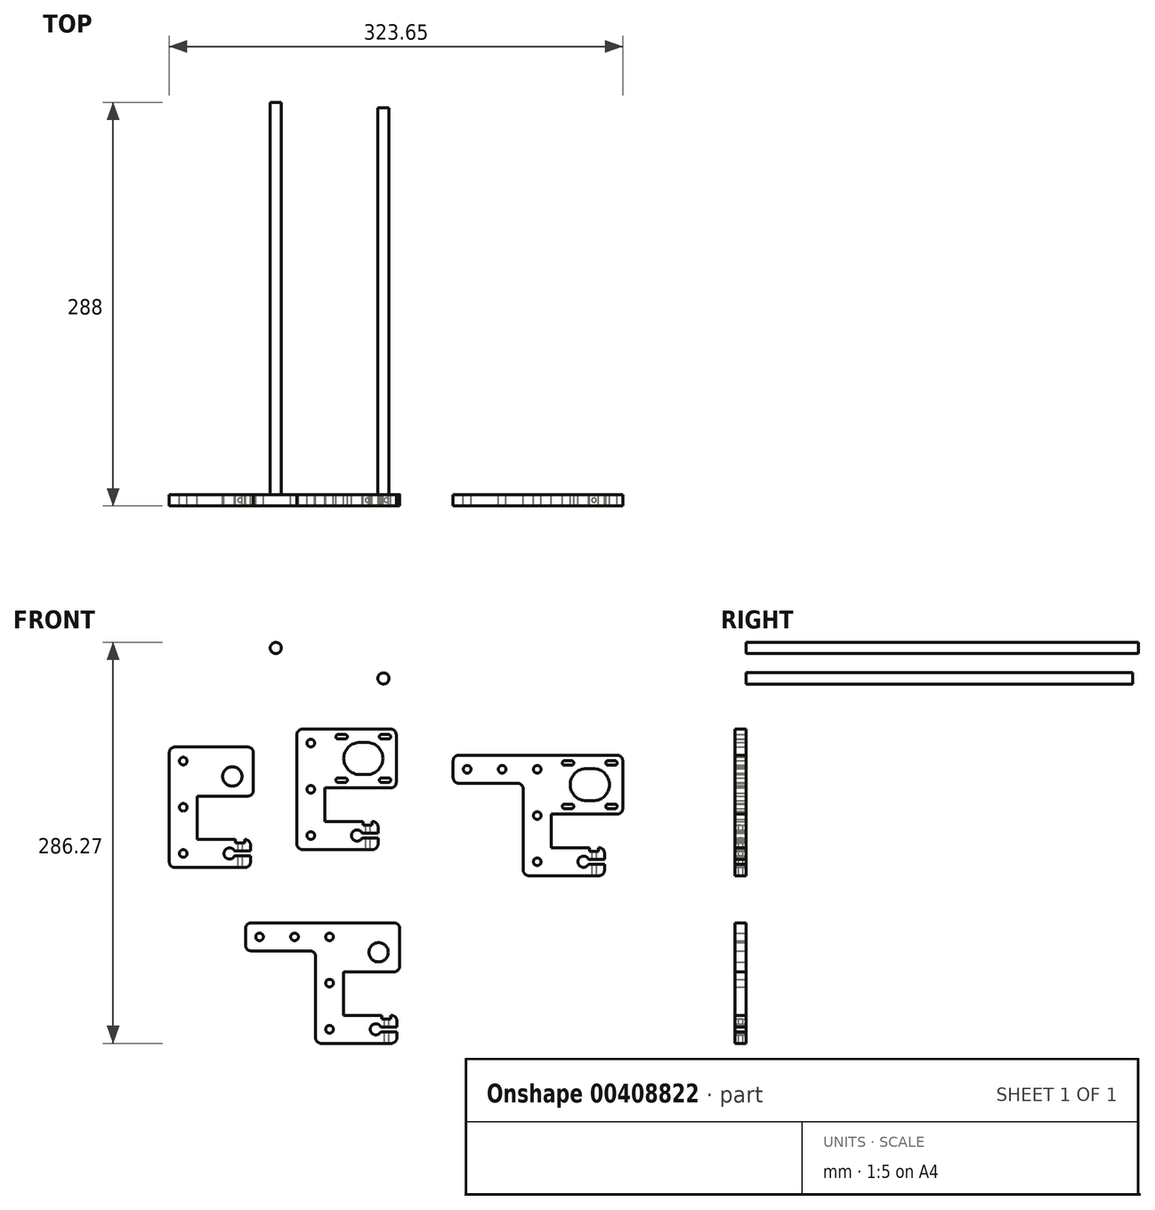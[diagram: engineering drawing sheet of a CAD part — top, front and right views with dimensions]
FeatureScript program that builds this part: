
annotation { "Feature Type Name" : "Feature", "Feature Type Description" : "" }
export const myFeature = defineFeature(function(context is Context, id is Id, definition is map)
    precondition{}
    {
        {
            var Q0;
            Q0=qCreatedBy(makeId("Front.planeOp"),FACE);
            var sketch = newSketch(context, id + "F0", { "sketchPlane" : qUnion([Q0])});
            skLineSegment(sketch, "E0", {"start": v(-154.16, 11) * mm, "end": v(-154.16, -55) * mm, "construction": true});
            skLineSegment(sketch, "E1", {"start": v(-179.8, 0) * mm, "end": v(-87.6, 0) * mm, "construction": true});
            skLineSegment(sketch, "E2", {"start": v(-97.16, 21) * mm, "end": v(-160.16, 21) * mm});
            skLineSegment(sketch, "E3", {"start": v(-164.16, 17) * mm, "end": v(-164.16, -61) * mm});
            skLineSegment(sketch, "E4", {"start": v(-160.16, -65) * mm, "end": v(-110.16, -65) * mm});
            skLineSegment(sketch, "E5", {"start": v(-106.16, -61) * mm, "end": v(-106.16, -56.75) * mm});
            skLineSegment(sketch, "E6", {"start": v(-93.16, 17) * mm, "end": v(-93.16, -17) * mm});
            skLineSegment(sketch, "E7", {"start": v(-97.16, -21) * mm, "end": v(-144.16, -21) * mm});
            skLineSegment(sketch, "E8", {"start": v(-144.16, -21) * mm, "end": v(-144.16, -45) * mm});
            skLineSegment(sketch, "E9", {"start": v(-144.16, -45) * mm, "end": v(-110.16, -45) * mm});
            skLineSegment(sketch, "E10", {"start": v(-106.16, -49) * mm, "end": v(-106.16, -53.25) * mm});
            skLineSegment(sketch, "E11", {"start": v(-142.74, -55) * mm, "end": v(-86.15, -55) * mm, "construction": true});
            skLineSegment(sketch, "E12", {"start": v(-106.16, -53.25) * mm, "end": v(-117.56, -53.25) * mm});
            skLineSegment(sketch, "E13", {"start": v(-106.16, -56.75) * mm, "end": v(-117.56, -56.75) * mm});
            skArc(sketch, "E14", {"start": v(-117.56, -53.25) * mm, "mid": v(-125.16, -55) * mm, "end": v(-117.56, -56.75) * mm});
            skCircle(sketch, "E15", {"center": v(-154.16, 11) * mm, "radius": 2.75 * mm});
            skCircle(sketch, "E16", {"center": v(-154.16, -22) * mm, "radius": 2.75 * mm});
            skCircle(sketch, "E17", {"center": v(-154.16, -55) * mm, "radius": 2.75 * mm});
            skLineSegment(sketch, "E18", {"start": v(-119.16, 0) * mm, "end": v(-114.16, 0) * mm, "construction": true});
            skArc(sketch, "E19.0.startCap", {"start": v(-119.16, -11.5) * mm, "mid": v(-130.66, 0) * mm, "end": v(-119.16, 11.5) * mm});
            skArc(sketch, "E19.0.endCap", {"start": v(-114.16, 11.5) * mm, "mid": v(-102.66, 0) * mm, "end": v(-114.16, -11.5) * mm});
            skLineSegment(sketch, "E19.0.left", {"start": v(-119.16, 11.5) * mm, "end": v(-114.16, 11.5) * mm});
            skLineSegment(sketch, "E19.0.right", {"start": v(-119.16, -11.5) * mm, "end": v(-114.16, -11.5) * mm});
            skPoint(sketch, "E20.visualSharp", {"position": v(-164.16, 21) * mm});
            skArc(sketch, "E20.filletArc", {"start": v(-160.16, 21) * mm, "mid": v(-162.99, 19.83) * mm, "end": v(-164.16, 17) * mm});
            skPoint(sketch, "E21.visualSharp", {"position": v(-93.16, 21) * mm});
            skArc(sketch, "E21.filletArc", {"start": v(-93.16, 17) * mm, "mid": v(-94.33, 19.83) * mm, "end": v(-97.16, 21) * mm});
            skPoint(sketch, "E22.visualSharp", {"position": v(-93.16, -21) * mm});
            skArc(sketch, "E22.filletArc", {"start": v(-97.16, -21) * mm, "mid": v(-94.33, -19.83) * mm, "end": v(-93.16, -17) * mm});
            skPoint(sketch, "E23.visualSharp", {"position": v(-106.16, -45) * mm});
            skArc(sketch, "E23.filletArc", {"start": v(-106.16, -49) * mm, "mid": v(-107.33, -46.17) * mm, "end": v(-110.16, -45) * mm});
            skPoint(sketch, "E24.visualSharp", {"position": v(-106.16, -65) * mm});
            skArc(sketch, "E24.filletArc", {"start": v(-110.16, -65) * mm, "mid": v(-107.33, -63.83) * mm, "end": v(-106.16, -61) * mm});
            skPoint(sketch, "E25.visualSharp", {"position": v(-164.16, -65) * mm});
            skArc(sketch, "E25.filletArc", {"start": v(-164.16, -61) * mm, "mid": v(-162.99, -63.83) * mm, "end": v(-160.16, -65) * mm});
            skLineSegment(sketch, "E26", {"start": v(-103.66, 15.5) * mm, "end": v(-98.66, 15.5) * mm, "construction": true});
            skArc(sketch, "E27.0.startCap", {"start": v(-103.66, 13.9) * mm, "mid": v(-105.26, 15.5) * mm, "end": v(-103.66, 17.1) * mm});
            skArc(sketch, "E27.0.endCap", {"start": v(-98.66, 17.1) * mm, "mid": v(-97.06, 15.5) * mm, "end": v(-98.66, 13.9) * mm});
            skLineSegment(sketch, "E27.0.left", {"start": v(-103.66, 17.1) * mm, "end": v(-98.66, 17.1) * mm});
            skLineSegment(sketch, "E27.0.right", {"start": v(-103.66, 13.9) * mm, "end": v(-98.66, 13.9) * mm});
            skLineSegment(sketch, "E28", {"start": v(-114.16, 23) * mm, "end": v(-114.16, -15.65) * mm, "construction": true});
            skLineSegment(sketch, "E29", {"start": v(-116.66, -11.5) * mm, "end": v(-116.66, 11.5) * mm, "construction": true});
            skArc(sketch, "E30.MirrorCS", {"start": v(-129.66, 13.9) * mm, "mid": v(-128.06, 15.5) * mm, "end": v(-129.66, 17.1) * mm});
            skArc(sketch, "E31.MirrorCS", {"start": v(-134.66, 17.1) * mm, "mid": v(-136.26, 15.5) * mm, "end": v(-134.66, 13.9) * mm});
            skLineSegment(sketch, "E32.MirrorCS", {"start": v(-129.66, 13.9) * mm, "end": v(-134.66, 13.9) * mm});
            skLineSegment(sketch, "E33.MirrorCS", {"start": v(-129.66, 15.5) * mm, "end": v(-134.66, 15.5) * mm, "construction": true});
            skLineSegment(sketch, "E34.MirrorCS", {"start": v(-129.66, 17.1) * mm, "end": v(-134.66, 17.1) * mm});
            skLineSegment(sketch, "E35.MirrorCS", {"start": v(-103.66, -13.9) * mm, "end": v(-98.66, -13.9) * mm});
            skArc(sketch, "E36.MirrorCS", {"start": v(-98.66, -17.1) * mm, "mid": v(-97.06, -15.5) * mm, "end": v(-98.66, -13.9) * mm});
            skArc(sketch, "E37.MirrorCS", {"start": v(-129.66, -13.9) * mm, "mid": v(-128.06, -15.5) * mm, "end": v(-129.66, -17.1) * mm});
            skLineSegment(sketch, "E38.MirrorCS", {"start": v(-103.66, -17.1) * mm, "end": v(-98.66, -17.1) * mm});
            skArc(sketch, "E39.MirrorCS", {"start": v(-134.66, -17.1) * mm, "mid": v(-136.26, -15.5) * mm, "end": v(-134.66, -13.9) * mm});
            skArc(sketch, "E40.MirrorCS", {"start": v(-103.66, -13.9) * mm, "mid": v(-105.26, -15.5) * mm, "end": v(-103.66, -17.1) * mm});
            skLineSegment(sketch, "E41.MirrorCS", {"start": v(-103.66, -15.5) * mm, "end": v(-98.66, -15.5) * mm, "construction": true});
            skLineSegment(sketch, "E42.MirrorCS", {"start": v(-129.66, -13.9) * mm, "end": v(-134.66, -13.9) * mm});
            skLineSegment(sketch, "E43.MirrorCS", {"start": v(-129.66, -15.5) * mm, "end": v(-134.66, -15.5) * mm, "construction": true});
            skLineSegment(sketch, "E44.MirrorCS", {"start": v(-129.66, -17.1) * mm, "end": v(-134.66, -17.1) * mm});
            skSolve(sketch);
        }
        {
            var Q0;
            Q0 = qSketchRegion(id + "F0", true);
            var Q1;
            Q1=makeQuery(id+"F0.imprint","IMPRINT",FACE,{"disambiguationData":[TD([[makeQuery(id+"F0.imprint","IMPRINT",EDGE,{"derivedFrom":sQuery(id+"F0.wireOp",EDGE,"E2")}),1.0]])]});
            extrude(context, id + "F1", {"entities" : qUnion([Q0, Q1]), "depth" : 8 * mm});
        }
        {
            var Q0;
            Q0=makeQuery(id+"F1.opExtrude","SWEPT_FACE",FACE,{"disambiguationData":[OSD([sQuery(id+"F0.wireOp",EDGE,"E4")])]});
            var sketch = newSketch(context, id + "F2", { "sketchPlane" : qUnion([Q0])});
            skLineSegment(sketch, "E45", {"start": v(-160.16, 4) * mm, "end": v(-110.16, 4) * mm, "construction": true});
            skCircle(sketch, "E46", {"center": v(-113.66, 4) * mm, "radius": 1.6 * mm});
            skSolve(sketch);
        }
        {
            var Q0;
            Q0 = qSketchRegion(id + "F2", true);
            var Q1;
            Q1=makeQuery(id+"F1.opExtrude","SWEPT_FACE",FACE,{"disambiguationData":[OSD([sQuery(id+"F0.wireOp",EDGE,"E9")])]});
            extrude(context, id + "F3", {"entities" : qUnion([Q0]), "operationType" : NewBodyOperationType.REMOVE, "endBound" : BoundingType.UP_TO_SURFACE, "oppositeDirection" : true, "endBoundEntityFace" : qUnion([Q1]), "depth" : 25 * mm});
        }
        {
            var Q0;
            Q0=makeQuery(id+"F1.opExtrude","SWEPT_FACE",FACE,{"disambiguationData":[OSD([sQuery(id+"F0.wireOp",EDGE,"E9")])]});
            var sketch = newSketch(context, id + "F4", { "sketchPlane" : qUnion([Q0])});
            skCircle(sketch, "E47.0", {"center": v(-113.66, -4) * mm, "radius": 1.6 * mm, "construction": true});
            skLineSegment(sketch, "E48.bottom", {"start": v(-110.4, -8) * mm, "end": v(-116.9, -8) * mm});
            skLineSegment(sketch, "E48.top", {"start": v(-110.4, 0) * mm, "end": v(-116.9, 0) * mm});
            skLineSegment(sketch, "E48.left", {"start": v(-110.4, -8) * mm, "end": v(-110.4, 0) * mm});
            skLineSegment(sketch, "E48.right", {"start": v(-116.9, -8) * mm, "end": v(-116.9, 0) * mm});
            skSolve(sketch);
        }
        {
            var Q0;
            Q0 = qSketchRegion(id + "F4", true);
            extrude(context, id + "F5", {"entities" : qUnion([Q0]), "operationType" : NewBodyOperationType.REMOVE, "oppositeDirection" : true, "depth" : 2.5 * mm});
        }
        {
            var Q0;
            Q0=qCreatedBy(makeId("Front.planeOp"),FACE);
            var sketch = newSketch(context, id + "F6", { "sketchPlane" : qUnion([Q0])});
            skLineSegment(sketch, "E49", {"start": v(-255.63, -1.84) * mm, "end": v(-201.41, -1.84) * mm, "construction": true});
            skLineSegment(sketch, "E50", {"start": v(-245.19, -1.84) * mm, "end": v(-245.19, -67.84) * mm, "construction": true});
            skLineSegment(sketch, "E51", {"start": v(-199.19, 8.16) * mm, "end": v(-251.19, 8.16) * mm});
            skLineSegment(sketch, "E52", {"start": v(-255.19, 4.16) * mm, "end": v(-255.19, -73.84) * mm});
            skLineSegment(sketch, "E53", {"start": v(-251.19, -77.84) * mm, "end": v(-201.19, -77.84) * mm});
            skLineSegment(sketch, "E54", {"start": v(-197.19, -73.84) * mm, "end": v(-197.19, -69.59) * mm});
            skLineSegment(sketch, "E55", {"start": v(-197.19, -69.59) * mm, "end": v(-208.59, -69.59) * mm});
            skLineSegment(sketch, "E56", {"start": v(-208.59, -66.09) * mm, "end": v(-197.19, -66.09) * mm});
            skLineSegment(sketch, "E57", {"start": v(-197.19, -66.09) * mm, "end": v(-197.19, -61.84) * mm});
            skLineSegment(sketch, "E58", {"start": v(-201.19, -57.84) * mm, "end": v(-235.19, -57.84) * mm});
            skLineSegment(sketch, "E59", {"start": v(-235.19, -57.84) * mm, "end": v(-235.19, -26.84) * mm});
            skLineSegment(sketch, "E60", {"start": v(-235.19, -26.84) * mm, "end": v(-199.19, -26.84) * mm});
            skLineSegment(sketch, "E61", {"start": v(-195.19, -22.84) * mm, "end": v(-195.19, 4.16) * mm});
            skLineSegment(sketch, "E62", {"start": v(-232.55, -67.84) * mm, "end": v(-177.18, -67.84) * mm, "construction": true});
            skArc(sketch, "E63", {"start": v(-208.59, -66.09) * mm, "mid": v(-216.19, -67.84) * mm, "end": v(-208.59, -69.59) * mm});
            skCircle(sketch, "E64", {"center": v(-245.19, -67.84) * mm, "radius": 2.75 * mm});
            skCircle(sketch, "E65", {"center": v(-245.19, -34.84) * mm, "radius": 2.75 * mm});
            skCircle(sketch, "E66", {"center": v(-245.19, -1.84) * mm, "radius": 2.75 * mm});
            skCircle(sketch, "E67", {"center": v(-210.19, -12.84) * mm, "radius": 6.9 * mm});
            skPoint(sketch, "E68.visualSharp", {"position": v(-255.19, 8.16) * mm});
            skArc(sketch, "E68.filletArc", {"start": v(-251.19, 8.16) * mm, "mid": v(-254.01, 6.99) * mm, "end": v(-255.19, 4.16) * mm});
            skPoint(sketch, "E69.visualSharp", {"position": v(-255.19, -77.84) * mm});
            skArc(sketch, "E69.filletArc", {"start": v(-255.19, -73.84) * mm, "mid": v(-254.01, -76.67) * mm, "end": v(-251.19, -77.84) * mm});
            skPoint(sketch, "E70.visualSharp", {"position": v(-197.19, -77.84) * mm});
            skArc(sketch, "E70.filletArc", {"start": v(-201.19, -77.84) * mm, "mid": v(-198.36, -76.67) * mm, "end": v(-197.19, -73.84) * mm});
            skPoint(sketch, "E71.visualSharp", {"position": v(-197.19, -57.84) * mm});
            skArc(sketch, "E71.filletArc", {"start": v(-197.19, -61.84) * mm, "mid": v(-198.36, -59.01) * mm, "end": v(-201.19, -57.84) * mm});
            skPoint(sketch, "E72.visualSharp", {"position": v(-195.19, -26.84) * mm});
            skArc(sketch, "E72.filletArc", {"start": v(-199.19, -26.84) * mm, "mid": v(-196.36, -25.67) * mm, "end": v(-195.19, -22.84) * mm});
            skPoint(sketch, "E73.visualSharp", {"position": v(-195.19, 8.16) * mm});
            skArc(sketch, "E73.filletArc", {"start": v(-195.19, 4.16) * mm, "mid": v(-196.36, 6.99) * mm, "end": v(-199.19, 8.16) * mm});
            skSolve(sketch);
        }
        {
            var Q0;
            Q0 = qSketchRegion(id + "F6", true);
            extrude(context, id + "F7", {"entities" : qUnion([Q0]), "depth" : 8 * mm});
        }
        {
            var Q0;
            Q0=makeQuery(id+"F7.opExtrude","SWEPT_FACE",FACE,{"disambiguationData":[OSD([sQuery(id+"F6.wireOp",EDGE,"E53")])]});
            var sketch = newSketch(context, id + "F8", { "sketchPlane" : qUnion([Q0])});
            skCircle(sketch, "E74", {"center": v(-204.69, 4) * mm, "radius": 1.6 * mm});
            skSolve(sketch);
        }
        {
            var Q0;
            Q0 = qSketchRegion(id + "F8", true);
            var Q1;
            Q1=makeQuery(id+"F7.opExtrude","SWEPT_FACE",FACE,{"disambiguationData":[OSD([sQuery(id+"F6.wireOp",EDGE,"E58")])]});
            extrude(context, id + "F9", {"entities" : qUnion([Q0]), "operationType" : NewBodyOperationType.REMOVE, "endBound" : BoundingType.UP_TO_SURFACE, "oppositeDirection" : true, "endBoundEntityFace" : qUnion([Q1]), "depth" : 25 * mm});
        }
        {
            var Q0;
            Q0=makeQuery(id+"F7.opExtrude","SWEPT_FACE",FACE,{"disambiguationData":[OSD([sQuery(id+"F6.wireOp",EDGE,"E58")])]});
            var sketch = newSketch(context, id + "F10", { "sketchPlane" : qUnion([Q0])});
            skCircle(sketch, "E75.0", {"center": v(-204.69, -4) * mm, "radius": 1.6 * mm});
            skLineSegment(sketch, "E76.bottom", {"start": v(-201.44, -8) * mm, "end": v(-207.94, -8) * mm});
            skLineSegment(sketch, "E76.top", {"start": v(-201.44, 0) * mm, "end": v(-207.94, 0) * mm});
            skLineSegment(sketch, "E76.left", {"start": v(-201.44, -8) * mm, "end": v(-201.44, 0) * mm});
            skLineSegment(sketch, "E76.right", {"start": v(-207.94, -8) * mm, "end": v(-207.94, 0) * mm});
            skSolve(sketch);
        }
        {
            var Q0;
            Q0 = qSketchRegion(id + "F10", true);
            extrude(context, id + "F11", {"entities" : qUnion([Q0]), "operationType" : NewBodyOperationType.REMOVE, "oppositeDirection" : true, "depth" : 2.5 * mm});
        }
        {
            var Q0;
            Q0=qCreatedBy(makeId("Front.planeOp"),FACE);
            var sketch = newSketch(context, id + "F12", { "sketchPlane" : qUnion([Q0])});
            skLineSegment(sketch, "E77", {"start": v(7.46, -7.7) * mm, "end": v(7.46, -73.7) * mm, "construction": true});
            skLineSegment(sketch, "E78", {"start": v(-18.18, -18.7) * mm, "end": v(74.02, -18.7) * mm, "construction": true});
            skLineSegment(sketch, "E79", {"start": v(64.46, 2.3) * mm, "end": v(-48.54, 2.3) * mm});
            skLineSegment(sketch, "E80", {"start": v(1.46, -83.7) * mm, "end": v(51.46, -83.7) * mm});
            skLineSegment(sketch, "E81", {"start": v(55.46, -79.7) * mm, "end": v(55.46, -75.46) * mm});
            skLineSegment(sketch, "E82", {"start": v(68.46, -1.7) * mm, "end": v(68.46, -35.7) * mm});
            skLineSegment(sketch, "E83", {"start": v(64.46, -39.7) * mm, "end": v(17.46, -39.7) * mm});
            skLineSegment(sketch, "E84", {"start": v(17.46, -39.7) * mm, "end": v(17.46, -63.7) * mm});
            skLineSegment(sketch, "E85", {"start": v(17.46, -63.7) * mm, "end": v(51.46, -63.7) * mm});
            skLineSegment(sketch, "E86", {"start": v(55.46, -67.7) * mm, "end": v(55.46, -71.96) * mm});
            skLineSegment(sketch, "E87", {"start": v(18.88, -73.7) * mm, "end": v(75.47, -73.7) * mm, "construction": true});
            skLineSegment(sketch, "E88", {"start": v(55.46, -71.96) * mm, "end": v(44.06, -71.96) * mm});
            skLineSegment(sketch, "E89", {"start": v(55.46, -75.46) * mm, "end": v(44.06, -75.46) * mm});
            skArc(sketch, "E90", {"start": v(44.06, -71.96) * mm, "mid": v(36.46, -73.7) * mm, "end": v(44.06, -75.46) * mm});
            skCircle(sketch, "E91", {"center": v(7.46, -7.7) * mm, "radius": 2.75 * mm});
            skCircle(sketch, "E92", {"center": v(7.46, -40.7) * mm, "radius": 2.75 * mm});
            skCircle(sketch, "E93", {"center": v(7.46, -73.7) * mm, "radius": 2.75 * mm});
            skLineSegment(sketch, "E94", {"start": v(42.46, -18.7) * mm, "end": v(47.46, -18.7) * mm, "construction": true});
            skArc(sketch, "E95.0.startCap", {"start": v(42.46, -30.2) * mm, "mid": v(30.96, -18.7) * mm, "end": v(42.46, -7.2) * mm});
            skArc(sketch, "E95.0.endCap", {"start": v(47.46, -7.2) * mm, "mid": v(58.96, -18.7) * mm, "end": v(47.46, -30.2) * mm});
            skLineSegment(sketch, "E95.0.left", {"start": v(42.46, -7.2) * mm, "end": v(47.46, -7.2) * mm});
            skLineSegment(sketch, "E95.0.right", {"start": v(42.46, -30.2) * mm, "end": v(47.46, -30.2) * mm});
            skPoint(sketch, "E96.visualSharp", {"position": v(68.46, 2.3) * mm});
            skArc(sketch, "E96.filletArc", {"start": v(68.46, -1.7) * mm, "mid": v(67.3, 1.12) * mm, "end": v(64.46, 2.3) * mm});
            skPoint(sketch, "E97.visualSharp", {"position": v(68.46, -39.7) * mm});
            skArc(sketch, "E97.filletArc", {"start": v(64.46, -39.7) * mm, "mid": v(67.3, -38.54) * mm, "end": v(68.46, -35.7) * mm});
            skPoint(sketch, "E98.visualSharp", {"position": v(55.46, -63.7) * mm});
            skArc(sketch, "E98.filletArc", {"start": v(55.46, -67.7) * mm, "mid": v(54.3, -64.88) * mm, "end": v(51.46, -63.7) * mm});
            skPoint(sketch, "E99.visualSharp", {"position": v(55.46, -83.7) * mm});
            skArc(sketch, "E99.filletArc", {"start": v(51.46, -83.7) * mm, "mid": v(54.3, -82.54) * mm, "end": v(55.46, -79.7) * mm});
            skLineSegment(sketch, "E100", {"start": v(57.96, -3.2) * mm, "end": v(62.96, -3.2) * mm, "construction": true});
            skArc(sketch, "E101.0.startCap", {"start": v(57.96, -4.8) * mm, "mid": v(56.36, -3.2) * mm, "end": v(57.96, -1.6) * mm});
            skArc(sketch, "E101.0.endCap", {"start": v(62.96, -1.6) * mm, "mid": v(64.56, -3.2) * mm, "end": v(62.96, -4.8) * mm});
            skLineSegment(sketch, "E101.0.left", {"start": v(57.96, -1.6) * mm, "end": v(62.96, -1.6) * mm});
            skLineSegment(sketch, "E101.0.right", {"start": v(57.96, -4.8) * mm, "end": v(62.96, -4.8) * mm});
            skLineSegment(sketch, "E102", {"start": v(47.46, 4.29) * mm, "end": v(47.46, -34.36) * mm, "construction": true});
            skLineSegment(sketch, "E103", {"start": v(-2.54, -21.7) * mm, "end": v(-2.54, -79.7) * mm});
            skLineSegment(sketch, "E104", {"start": v(-52.54, -1.7) * mm, "end": v(-52.54, -13.7) * mm});
            skLineSegment(sketch, "E105", {"start": v(-48.54, -17.7) * mm, "end": v(-6.54, -17.7) * mm});
            skCircle(sketch, "E106", {"center": v(-42.54, -7.7) * mm, "radius": 2.75 * mm});
            skCircle(sketch, "E107", {"center": v(-17.54, -7.7) * mm, "radius": 2.75 * mm});
            skPoint(sketch, "E108.visualSharp", {"position": v(-52.54, 2.3) * mm});
            skArc(sketch, "E108.filletArc", {"start": v(-48.54, 2.3) * mm, "mid": v(-51.37, 1.12) * mm, "end": v(-52.54, -1.7) * mm});
            skPoint(sketch, "E109.visualSharp", {"position": v(-52.54, -17.7) * mm});
            skArc(sketch, "E109.filletArc", {"start": v(-52.54, -13.7) * mm, "mid": v(-51.37, -16.54) * mm, "end": v(-48.54, -17.7) * mm});
            skPoint(sketch, "E110.visualSharp", {"position": v(-2.54, -17.7) * mm});
            skArc(sketch, "E110.filletArc", {"start": v(-2.54, -21.7) * mm, "mid": v(-3.7, -18.88) * mm, "end": v(-6.54, -17.7) * mm});
            skPoint(sketch, "E111.visualSharp", {"position": v(-2.54, -83.7) * mm});
            skArc(sketch, "E111.filletArc", {"start": v(-2.54, -79.7) * mm, "mid": v(-1.37, -82.54) * mm, "end": v(1.46, -83.7) * mm});
            skLineSegment(sketch, "E112", {"start": v(44.96, -30.2) * mm, "end": v(44.96, -7.2) * mm, "construction": true});
            skLineSegment(sketch, "E113.MirrorCS", {"start": v(31.96, -1.6) * mm, "end": v(26.96, -1.6) * mm});
            skLineSegment(sketch, "E114.MirrorCS", {"start": v(31.96, -3.2) * mm, "end": v(26.96, -3.2) * mm, "construction": true});
            skArc(sketch, "E115.MirrorCS", {"start": v(31.96, -4.8) * mm, "mid": v(33.56, -3.2) * mm, "end": v(31.96, -1.6) * mm});
            skArc(sketch, "E116.MirrorCS", {"start": v(26.96, -1.6) * mm, "mid": v(25.36, -3.2) * mm, "end": v(26.96, -4.8) * mm});
            skLineSegment(sketch, "E117.MirrorCS", {"start": v(31.96, -4.8) * mm, "end": v(26.96, -4.8) * mm});
            skLineSegment(sketch, "E118.MirrorCS", {"start": v(31.96, -35.8) * mm, "end": v(26.96, -35.8) * mm});
            skArc(sketch, "E119.MirrorCS", {"start": v(31.96, -32.6) * mm, "mid": v(33.56, -34.2) * mm, "end": v(31.96, -35.8) * mm});
            skArc(sketch, "E120.MirrorCS", {"start": v(62.96, -35.8) * mm, "mid": v(64.56, -34.2) * mm, "end": v(62.96, -32.6) * mm});
            skArc(sketch, "E121.MirrorCS", {"start": v(26.96, -35.8) * mm, "mid": v(25.36, -34.2) * mm, "end": v(26.96, -32.6) * mm});
            skLineSegment(sketch, "E122.MirrorCS", {"start": v(57.96, -35.8) * mm, "end": v(62.96, -35.8) * mm});
            skLineSegment(sketch, "E123.MirrorCS", {"start": v(57.96, -32.6) * mm, "end": v(62.96, -32.6) * mm});
            skLineSegment(sketch, "E124.MirrorCS", {"start": v(31.96, -34.2) * mm, "end": v(26.96, -34.2) * mm, "construction": true});
            skLineSegment(sketch, "E125.MirrorCS", {"start": v(31.96, -32.6) * mm, "end": v(26.96, -32.6) * mm});
            skLineSegment(sketch, "E126.MirrorCS", {"start": v(57.96, -34.2) * mm, "end": v(62.96, -34.2) * mm, "construction": true});
            skArc(sketch, "E127.MirrorCS", {"start": v(57.96, -32.6) * mm, "mid": v(56.36, -34.2) * mm, "end": v(57.96, -35.8) * mm});
            skSolve(sketch);
        }
        {
            var Q0;
            Q0=makeQuery(id+"F12.imprint","IMPRINT",FACE,{"disambiguationData":[TD([[makeQuery(id+"F12.imprint","IMPRINT",EDGE,{"derivedFrom":sQuery(id+"F12.wireOp",EDGE,"E79")}),1.0]])]});
            extrude(context, id + "F13", {"entities" : qUnion([Q0]), "depth" : 8 * mm});
        }
        {
            var Q0;
            Q0=makeQuery(id+"F13.opExtrude","SWEPT_FACE",FACE,{"disambiguationData":[OSD([sQuery(id+"F12.wireOp",EDGE,"E80")])]});
            var sketch = newSketch(context, id + "F14", { "sketchPlane" : qUnion([Q0])});
            skCircle(sketch, "E128", {"center": v(47.96, 4) * mm, "radius": 1.6 * mm});
            skSolve(sketch);
        }
        {
            var Q0;
            Q0 = qSketchRegion(id + "F14", true);
            var Q1;
            Q1=makeQuery(id+"F13.opExtrude","SWEPT_FACE",FACE,{"disambiguationData":[OSD([sQuery(id+"F12.wireOp",EDGE,"E85")])]});
            extrude(context, id + "F15", {"entities" : qUnion([Q0]), "operationType" : NewBodyOperationType.REMOVE, "endBound" : BoundingType.UP_TO_SURFACE, "oppositeDirection" : true, "endBoundEntityFace" : qUnion([Q1]), "depth" : 25 * mm});
        }
        {
            var Q0;
            Q0=makeQuery(id+"F13.opExtrude","SWEPT_FACE",FACE,{"disambiguationData":[OSD([sQuery(id+"F12.wireOp",EDGE,"E85")])]});
            var sketch = newSketch(context, id + "F16", { "sketchPlane" : qUnion([Q0])});
            skCircle(sketch, "E129.0", {"center": v(47.96, -4) * mm, "radius": 1.6 * mm});
            skLineSegment(sketch, "E130.bottom", {"start": v(51.21, -8) * mm, "end": v(44.71, -8) * mm});
            skLineSegment(sketch, "E130.top", {"start": v(51.21, 0) * mm, "end": v(44.71, 0) * mm});
            skLineSegment(sketch, "E130.left", {"start": v(51.21, -8) * mm, "end": v(51.21, 0) * mm});
            skLineSegment(sketch, "E130.right", {"start": v(44.71, -8) * mm, "end": v(44.71, 0) * mm});
            skSolve(sketch);
        }
        {
            var Q0;
            Q0=makeQuery(id+"F16.imprint","IMPRINT",FACE,{"disambiguationData":[TD([[makeQuery(id+"F16.imprint","IMPRINT",EDGE,{"derivedFrom":sQuery(id+"F16.wireOp",EDGE,"E129.0")}),1.0]])]});
            extrude(context, id + "F17", {"entities" : qUnion([Q0]), "operationType" : NewBodyOperationType.REMOVE, "oppositeDirection" : true, "depth" : 2.5 * mm});
        }
        {
            var Q0;
            Q0=qCreatedBy(makeId("Front.planeOp"),FACE);
            var sketch = newSketch(context, id + "F18", { "sketchPlane" : qUnion([Q0])});
            skLineSegment(sketch, "E131", {"start": v(-216.5, -127.36) * mm, "end": v(-97, -127.36) * mm, "construction": true});
            skLineSegment(sketch, "E132", {"start": v(-140.77, -127.36) * mm, "end": v(-140.77, -193.36) * mm, "construction": true});
            skLineSegment(sketch, "E133", {"start": v(-146.77, -203.36) * mm, "end": v(-96.77, -203.36) * mm});
            skLineSegment(sketch, "E134", {"start": v(-92.77, -199.36) * mm, "end": v(-92.77, -195.11) * mm});
            skLineSegment(sketch, "E135", {"start": v(-92.77, -195.11) * mm, "end": v(-104.17, -195.11) * mm});
            skLineSegment(sketch, "E136", {"start": v(-104.17, -191.61) * mm, "end": v(-92.77, -191.61) * mm});
            skLineSegment(sketch, "E137", {"start": v(-92.77, -191.61) * mm, "end": v(-92.77, -187.36) * mm});
            skLineSegment(sketch, "E138", {"start": v(-96.77, -183.36) * mm, "end": v(-130.77, -183.36) * mm});
            skLineSegment(sketch, "E139", {"start": v(-130.77, -183.36) * mm, "end": v(-130.77, -152.36) * mm});
            skLineSegment(sketch, "E140", {"start": v(-130.77, -152.36) * mm, "end": v(-94.77, -152.36) * mm});
            skLineSegment(sketch, "E141", {"start": v(-90.77, -148.36) * mm, "end": v(-90.77, -121.36) * mm});
            skLineSegment(sketch, "E142", {"start": v(-128.13, -193.36) * mm, "end": v(-72.76, -193.36) * mm, "construction": true});
            skArc(sketch, "E143", {"start": v(-104.17, -191.61) * mm, "mid": v(-111.77, -193.36) * mm, "end": v(-104.17, -195.11) * mm});
            skCircle(sketch, "E144", {"center": v(-140.77, -193.36) * mm, "radius": 2.75 * mm});
            skCircle(sketch, "E145", {"center": v(-140.77, -160.36) * mm, "radius": 2.75 * mm});
            skCircle(sketch, "E146", {"center": v(-140.77, -127.36) * mm, "radius": 2.75 * mm});
            skCircle(sketch, "E147", {"center": v(-105.77, -138.36) * mm, "radius": 6.9 * mm});
            skPoint(sketch, "E148.visualSharp", {"position": v(-150.77, -203.36) * mm});
            skPoint(sketch, "E149.visualSharp", {"position": v(-92.77, -203.36) * mm});
            skArc(sketch, "E149.filletArc", {"start": v(-96.77, -203.36) * mm, "mid": v(-93.94, -202.2) * mm, "end": v(-92.77, -199.36) * mm});
            skPoint(sketch, "E150.visualSharp", {"position": v(-92.77, -183.36) * mm});
            skArc(sketch, "E150.filletArc", {"start": v(-92.77, -187.36) * mm, "mid": v(-93.94, -184.53) * mm, "end": v(-96.77, -183.36) * mm});
            skPoint(sketch, "E151.visualSharp", {"position": v(-90.77, -152.36) * mm});
            skArc(sketch, "E151.filletArc", {"start": v(-94.77, -152.36) * mm, "mid": v(-91.94, -151.2) * mm, "end": v(-90.77, -148.36) * mm});
            skLineSegment(sketch, "E152", {"start": v(-150.77, -141.36) * mm, "end": v(-150.77, -199.36) * mm});
            skLineSegment(sketch, "E153", {"start": v(-94.77, -117.36) * mm, "end": v(-196.77, -117.36) * mm});
            skLineSegment(sketch, "E154", {"start": v(-200.77, -121.36) * mm, "end": v(-200.77, -133.36) * mm});
            skLineSegment(sketch, "E155", {"start": v(-196.77, -137.36) * mm, "end": v(-154.77, -137.36) * mm});
            skCircle(sketch, "E156", {"center": v(-190.77, -127.36) * mm, "radius": 2.75 * mm});
            skCircle(sketch, "E157", {"center": v(-165.77, -127.36) * mm, "radius": 2.75 * mm});
            skPoint(sketch, "E158.visualSharp", {"position": v(-200.77, -117.36) * mm});
            skArc(sketch, "E158.filletArc", {"start": v(-196.77, -117.36) * mm, "mid": v(-199.6, -118.53) * mm, "end": v(-200.77, -121.36) * mm});
            skPoint(sketch, "E159.visualSharp", {"position": v(-200.77, -137.36) * mm});
            skArc(sketch, "E159.filletArc", {"start": v(-200.77, -133.36) * mm, "mid": v(-199.6, -136.2) * mm, "end": v(-196.77, -137.36) * mm});
            skPoint(sketch, "E160.visualSharp", {"position": v(-150.77, -137.36) * mm});
            skArc(sketch, "E160.filletArc", {"start": v(-150.77, -141.36) * mm, "mid": v(-151.94, -138.53) * mm, "end": v(-154.77, -137.36) * mm});
            skArc(sketch, "E161.filletArc", {"start": v(-150.77, -199.36) * mm, "mid": v(-149.6, -202.2) * mm, "end": v(-146.77, -203.36) * mm});
            skPoint(sketch, "E162.visualSharp", {"position": v(-90.77, -117.36) * mm});
            skArc(sketch, "E162.filletArc", {"start": v(-90.77, -121.36) * mm, "mid": v(-91.94, -118.53) * mm, "end": v(-94.77, -117.36) * mm});
            skSolve(sketch);
        }
        {
            var Q0;
            Q0=makeQuery(id+"F18.imprint","IMPRINT",FACE,{"disambiguationData":[TD([[makeQuery(id+"F18.imprint","IMPRINT",EDGE,{"derivedFrom":sQuery(id+"F18.wireOp",EDGE,"E133")}),1.0]])]});
            extrude(context, id + "F19", {"entities" : qUnion([Q0]), "depth" : 8 * mm});
        }
        {
            var Q0;
            Q0=makeQuery(id+"F19.opExtrude","SWEPT_FACE",FACE,{"disambiguationData":[OSD([sQuery(id+"F18.wireOp",EDGE,"E133")])]});
            var sketch = newSketch(context, id + "F20", { "sketchPlane" : qUnion([Q0])});
            skCircle(sketch, "E163", {"center": v(-100.27, 4) * mm, "radius": 1.6 * mm});
            skSolve(sketch);
        }
        {
            var Q0;
            Q0=makeQuery(id+"F20.imprint","IMPRINT",FACE,{"disambiguationData":[TD([[makeQuery(id+"F20.imprint","IMPRINT",EDGE,{"derivedFrom":sQuery(id+"F20.wireOp",EDGE,"E163")}),1.0]])]});
            var Q1;
            Q1=makeQuery(id+"F19.opExtrude","SWEPT_FACE",FACE,{"disambiguationData":[OSD([sQuery(id+"F18.wireOp",EDGE,"E138")])]});
            extrude(context, id + "F21", {"entities" : qUnion([Q0]), "operationType" : NewBodyOperationType.REMOVE, "endBound" : BoundingType.UP_TO_SURFACE, "oppositeDirection" : true, "endBoundEntityFace" : qUnion([Q1]), "depth" : 25 * mm});
        }
        {
            var Q0;
            Q0=makeQuery(id+"F19.opExtrude","SWEPT_FACE",FACE,{"disambiguationData":[OSD([sQuery(id+"F18.wireOp",EDGE,"E138")])]});
            var sketch = newSketch(context, id + "F22", { "sketchPlane" : qUnion([Q0])});
            skCircle(sketch, "E164.0", {"center": v(-100.27, -4) * mm, "radius": 1.6 * mm});
            skLineSegment(sketch, "E165.bottom", {"start": v(-97.02, -8) * mm, "end": v(-103.52, -8) * mm});
            skLineSegment(sketch, "E165.top", {"start": v(-97.02, 0) * mm, "end": v(-103.52, 0) * mm});
            skLineSegment(sketch, "E165.left", {"start": v(-97.02, -8) * mm, "end": v(-97.02, 0) * mm});
            skLineSegment(sketch, "E165.right", {"start": v(-103.52, -8) * mm, "end": v(-103.52, 0) * mm});
            skSolve(sketch);
        }
        {
            var Q0;
            Q0=makeQuery(id+"F22.imprint","IMPRINT",FACE,{"disambiguationData":[TD([[makeQuery(id+"F22.imprint","IMPRINT",EDGE,{"derivedFrom":sQuery(id+"F22.wireOp",EDGE,"E164.0")}),-1.0]])]});
            extrude(context, id + "F23", {"entities" : qUnion([Q0]), "operationType" : NewBodyOperationType.REMOVE, "oppositeDirection" : true, "depth" : 2.5 * mm});
        }
        {
            var Q0;
            Q0=qCreatedBy(makeId("Front.planeOp"),FACE);
            var sketch = newSketch(context, id + "F24", { "sketchPlane" : qUnion([Q0])});
            skCircle(sketch, "E166", {"center": v(-102.35, 57.16) * mm, "radius": 4 * mm});
            skSolve(sketch);
        }
        {
            var Q0;
            Q0=makeQuery(id+"F24.imprint","IMPRINT",FACE,{"disambiguationData":[TD([[makeQuery(id+"F24.imprint","IMPRINT",EDGE,{"derivedFrom":sQuery(id+"F24.wireOp",EDGE,"E166")}),1.0]])]});
            extrude(context, id + "F25", {"entities" : qUnion([Q0]), "oppositeDirection" : true, "depth" : 276 * mm});
        }
        {
            var Q0;
            Q0=qCreatedBy(makeId("Front.planeOp"),FACE);
            var sketch = newSketch(context, id + "F26", { "sketchPlane" : qUnion([Q0])});
            skCircle(sketch, "E167", {"center": v(-179.16, 78.91) * mm, "radius": 4 * mm});
            skSolve(sketch);
        }
        {
            var Q0;
            Q0=makeQuery(id+"F26.imprint","IMPRINT",FACE,{"disambiguationData":[TD([[makeQuery(id+"F26.imprint","IMPRINT",EDGE,{"derivedFrom":sQuery(id+"F26.wireOp",EDGE,"E167")}),1.0]])]});
            extrude(context, id + "F27", {"entities" : qUnion([Q0]), "oppositeDirection" : true, "depth" : 280 * mm});
        }
    });
